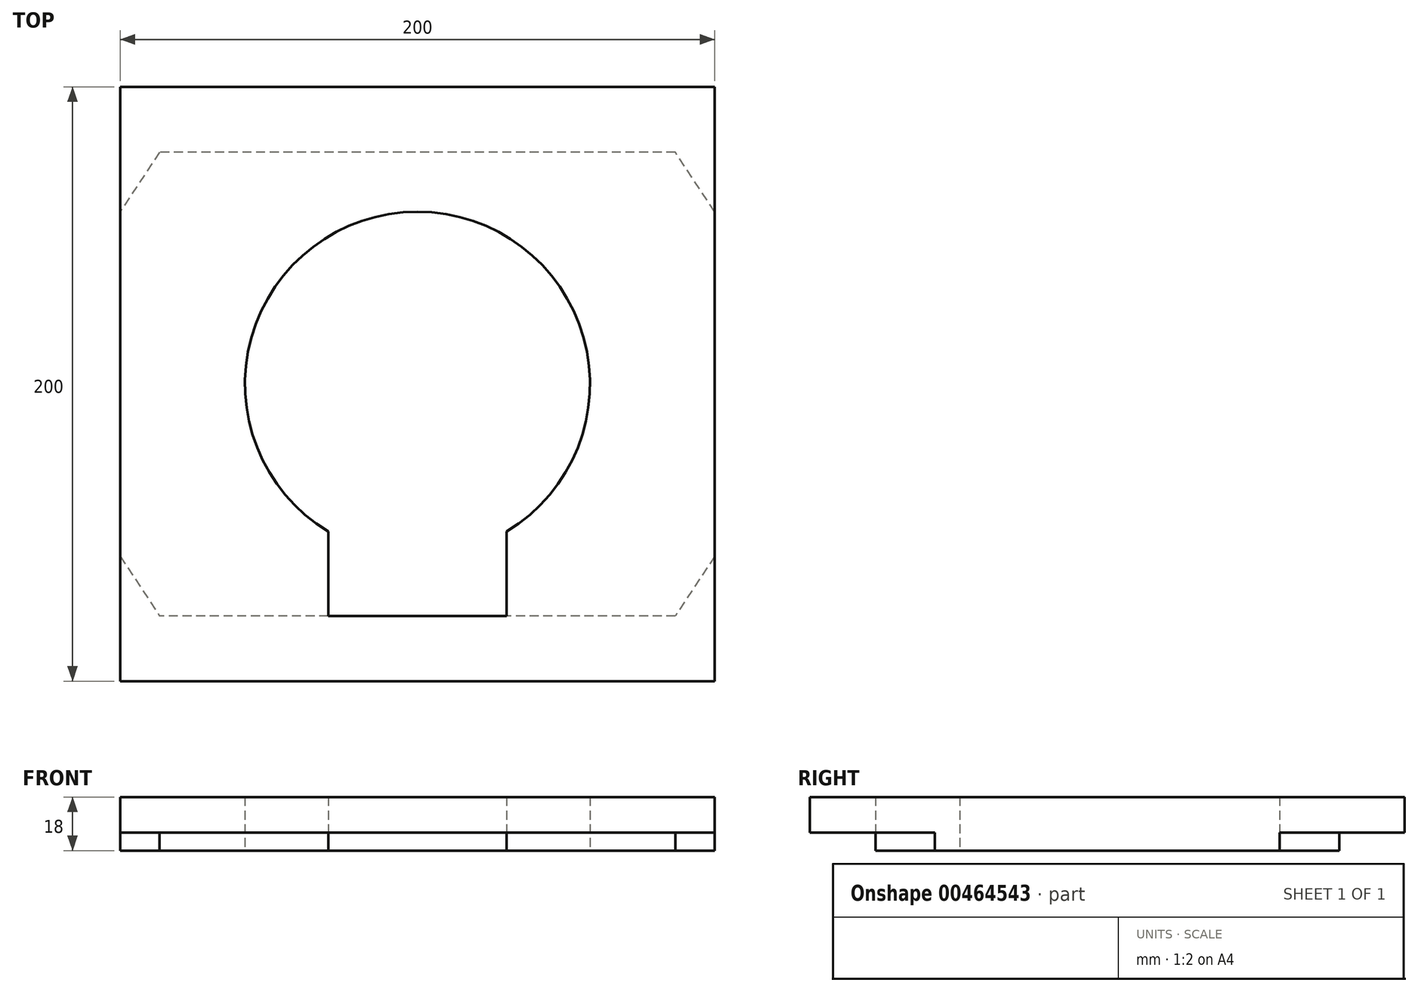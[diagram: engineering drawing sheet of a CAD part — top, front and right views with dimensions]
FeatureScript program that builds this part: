
annotation { "Feature Type Name" : "Feature", "Feature Type Description" : "" }
export const myFeature = defineFeature(function(context is Context, id is Id, definition is map)
    precondition{}
    {
        {
            var Q0;
            Q0=qCreatedBy(makeId("Top.planeOp"),FACE);
            var sketch = newSketch(context, id + "F0", { "sketchPlane" : qUnion([Q0])});
            skLineSegment(sketch, "E0.bottom", {"start": v(86.75, 78) * mm, "end": v(-86.75, 78) * mm});
            skLineSegment(sketch, "E0.top", {"start": v(86.75, -78) * mm, "end": v(30, -78) * mm});
            skLineSegment(sketch, "E0.left", {"start": v(100, 58) * mm, "end": v(100, -58) * mm});
            skLineSegment(sketch, "E0.right", {"start": v(-100, 58) * mm, "end": v(-100, -58) * mm});
            skPoint(sketch, "E0.middle", {"position": v(0, 0) * mm});
            skArc(sketch, "E1", {"start": v(30, -49.64) * mm, "mid": v(0, 58) * mm, "end": v(-30, -49.64) * mm});
            skLineSegment(sketch, "E2", {"start": v(-86.75, 78) * mm, "end": v(-100, 58) * mm});
            skLineSegment(sketch, "E3", {"start": v(-100, -58) * mm, "end": v(-86.75, -78) * mm});
            skLineSegment(sketch, "E4", {"start": v(100, -58) * mm, "end": v(86.75, -78) * mm});
            skLineSegment(sketch, "E5", {"start": v(100, 58) * mm, "end": v(86.75, 78) * mm});
            skPoint(sketch, "E6.orphan", {"position": v(-100, 78) * mm});
            skPoint(sketch, "E7.orphan", {"position": v(-100, -78) * mm});
            skPoint(sketch, "E8.orphan", {"position": v(100, -78) * mm});
            skPoint(sketch, "E9.orphan", {"position": v(100, 78) * mm});
            skPoint(sketch, "E10", {"position": v(-100, 0) * mm});
            skPoint(sketch, "E11", {"position": v(0, 78) * mm});
            skPoint(sketch, "E12", {"position": v(100, 0) * mm});
            skPoint(sketch, "E13", {"position": v(0, -78) * mm});
            skLineSegment(sketch, "E14", {"start": v(-30, -49.64) * mm, "end": v(-30, -78) * mm});
            skLineSegment(sketch, "E15", {"start": v(30, -49.64) * mm, "end": v(30, -78) * mm});
            skLineSegment(sketch, "E16.trimOffspring", {"start": v(-30, -78) * mm, "end": v(-86.75, -78) * mm});
            skLineSegment(sketch, "E17", {"start": v(-30, -78) * mm, "end": v(30, -78) * mm});
            skLineSegment(sketch, "E18.bottom", {"start": v(100, 100) * mm, "end": v(-100, 100) * mm});
            skLineSegment(sketch, "E18.top", {"start": v(100, -100) * mm, "end": v(-100, -100) * mm});
            skLineSegment(sketch, "E18.left", {"start": v(100, 100) * mm, "end": v(100, -100) * mm});
            skLineSegment(sketch, "E18.right", {"start": v(-100, 100) * mm, "end": v(-100, -100) * mm});
            skSolve(sketch);
        }
        {
            var Q0;
            Q0=makeQuery(id+"F0.imprint","IMPRINT",FACE,{"disambiguationData":[TD([[makeQuery(id+"F0.imprint","IMPRINT",EDGE,{"derivedFrom":sQuery(id+"F0.wireOp",EDGE,"E0.bottom")}),-1.0]])]});
            var Q1;
            Q1=makeQuery(id+"F0.imprint","IMPRINT",FACE,{"disambiguationData":[TD([[makeQuery(id+"F0.imprint","IMPRINT",EDGE,{"derivedFrom":sQuery(id+"F0.wireOp",EDGE,"E0.bottom")}),1.0]])]});
            var Q2;
            Q2=makeQuery(id+"F0.imprint","IMPRINT",FACE,{"disambiguationData":[TD([[makeQuery(id+"F0.imprint","IMPRINT",EDGE,{"derivedFrom":sQuery(id+"F0.wireOp",EDGE,"E0.top")}),1.0]])]});
            extrude(context, id + "F1", {"entities" : qUnion([Q0, Q1, Q2]), "depth" : 12 * mm, "offsetDistance" : 25 * mm});
        }
        {
            var Q0;
            Q0=makeQuery(id+"F0.imprint","IMPRINT",FACE,{"disambiguationData":[TD([[makeQuery(id+"F0.imprint","IMPRINT",EDGE,{"derivedFrom":sQuery(id+"F0.wireOp",EDGE,"E0.bottom")}),1.0]])]});
            extrude(context, id + "F2", {"entities" : qUnion([Q0]), "operationType" : NewBodyOperationType.ADD, "oppositeDirection" : true, "depth" : 6 * mm});
        }
    });
